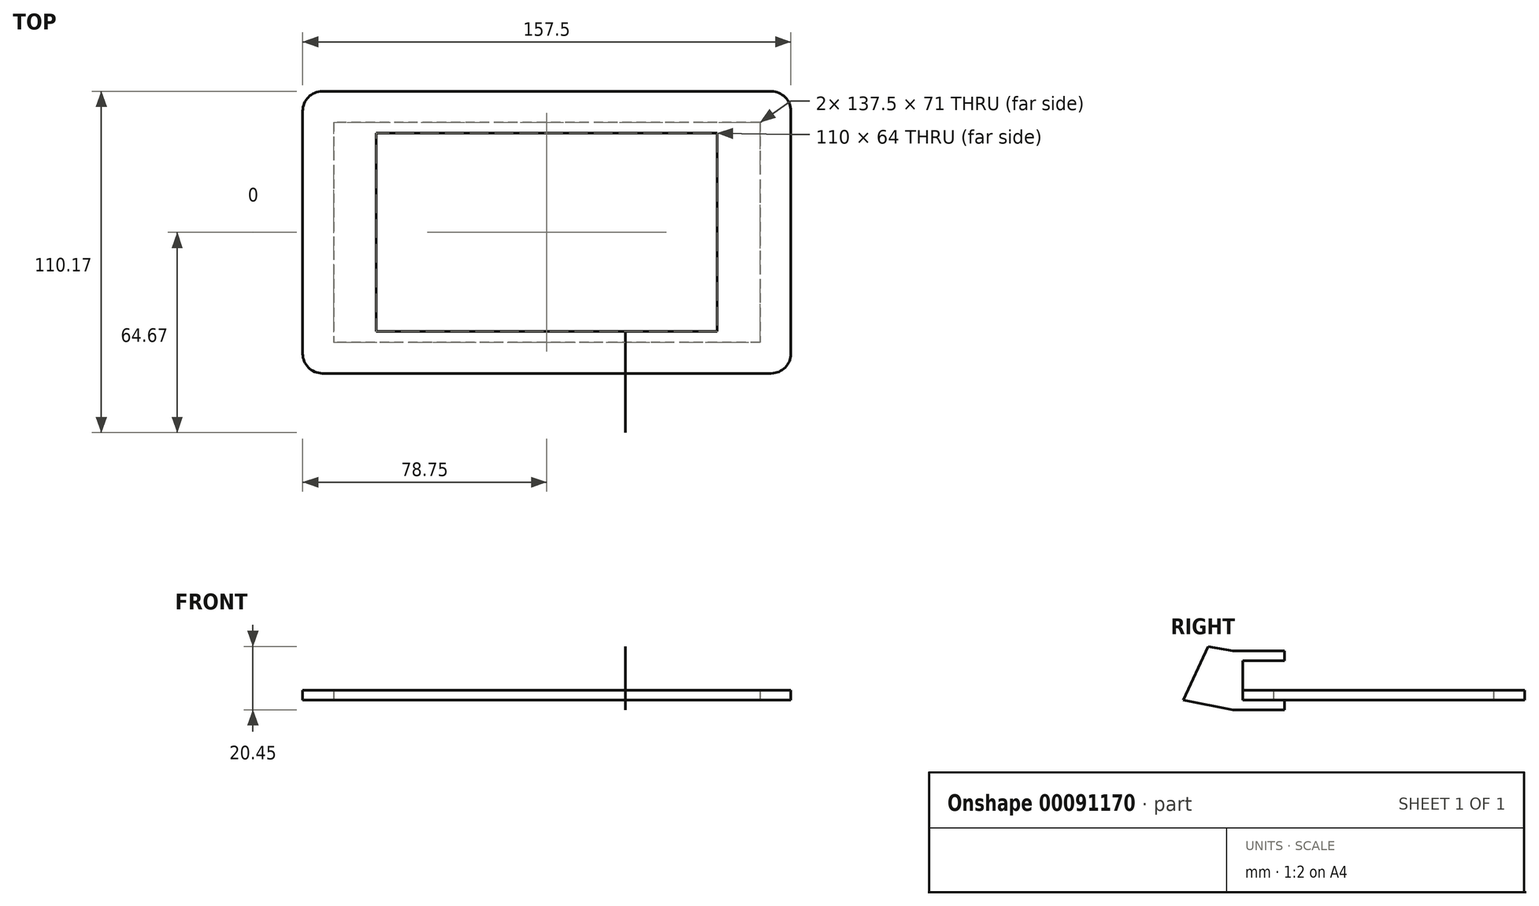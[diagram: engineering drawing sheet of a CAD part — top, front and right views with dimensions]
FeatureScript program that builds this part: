
annotation { "Feature Type Name" : "Feature", "Feature Type Description" : "" }
export const myFeature = defineFeature(function(context is Context, id is Id, definition is map)
    precondition{}
    {
        {
            var Q0;
            Q0=qCreatedBy(makeId("Top.planeOp"),FACE);
            var sketch = newSketch(context, id + "F0", { "sketchPlane" : qUnion([Q0])});
            skLineSegment(sketch, "E0.bottom", {"start": v(55, 32) * mm, "end": v(-55, 32) * mm});
            skLineSegment(sketch, "E0.top", {"start": v(55, -32) * mm, "end": v(-55, -32) * mm});
            skLineSegment(sketch, "E0.left", {"start": v(55, 32) * mm, "end": v(55, -32) * mm});
            skLineSegment(sketch, "E0.right", {"start": v(-55, 32) * mm, "end": v(-55, -32) * mm});
            skPoint(sketch, "E0.middle", {"position": v(0, 0) * mm});
            skLineSegment(sketch, "E1.bottom", {"start": v(68.75, 35.5) * mm, "end": v(-68.75, 35.5) * mm});
            skLineSegment(sketch, "E1.top", {"start": v(68.75, -35.5) * mm, "end": v(-68.75, -35.5) * mm});
            skLineSegment(sketch, "E1.left", {"start": v(68.75, 35.5) * mm, "end": v(68.75, -35.5) * mm});
            skLineSegment(sketch, "E1.right", {"start": v(-68.75, 35.5) * mm, "end": v(-68.75, -35.5) * mm});
            skLineSegment(sketch, "E2.bottom", {"start": v(72.4, 45.5) * mm, "end": v(-72.4, 45.5) * mm});
            skLineSegment(sketch, "E2.top", {"start": v(72.4, -45.5) * mm, "end": v(-72.4, -45.5) * mm});
            skLineSegment(sketch, "E2.left", {"start": v(78.75, 39.15) * mm, "end": v(78.75, -39.15) * mm});
            skLineSegment(sketch, "E2.right", {"start": v(-78.75, 39.15) * mm, "end": v(-78.75, -39.15) * mm});
            skLineSegment(sketch, "E3", {"start": v(0, -45.5) * mm, "end": v(0, -35.5) * mm});
            skLineSegment(sketch, "E4", {"start": v(68.75, 0) * mm, "end": v(78.75, 0) * mm});
            skLineSegment(sketch, "E5", {"start": v(0, 35.5) * mm, "end": v(0, 45.5) * mm});
            skLineSegment(sketch, "E6", {"start": v(-68.75, 0) * mm, "end": v(-78.75, 0) * mm});
            skPoint(sketch, "E7.visualSharp", {"position": v(-78.75, 45.5) * mm});
            skArc(sketch, "E7.filletArc", {"start": v(-72.4, 45.5) * mm, "mid": v(-76.9, 43.64) * mm, "end": v(-78.75, 39.15) * mm});
            skPoint(sketch, "E8.visualSharp", {"position": v(78.75, 45.5) * mm});
            skArc(sketch, "E8.filletArc", {"start": v(78.75, 39.15) * mm, "mid": v(76.9, 43.64) * mm, "end": v(72.4, 45.5) * mm});
            skPoint(sketch, "E9.visualSharp", {"position": v(78.75, -45.5) * mm});
            skArc(sketch, "E9.filletArc", {"start": v(72.4, -45.5) * mm, "mid": v(76.9, -43.64) * mm, "end": v(78.75, -39.15) * mm});
            skPoint(sketch, "E10.visualSharp", {"position": v(-78.75, -45.5) * mm});
            skArc(sketch, "E10.filletArc", {"start": v(-78.75, -39.15) * mm, "mid": v(-76.9, -43.64) * mm, "end": v(-72.4, -45.5) * mm});
            skSolve(sketch);
        }
        {
            var Q0;
            Q0 = qSketchRegion(id + "F0", true);
            var Q1;
            Q1=makeQuery(id+"F0.imprint","IMPRINT",FACE,{"disambiguationData":[TD([[makeQuery(id+"F0.imprint","IMPRINT",EDGE,{"derivedFrom":sQuery(id+"F0.wireOp",EDGE,"E0.bottom")}),-1.0]])]});
            var Q2;
            Q2=makeQuery(id+"F0.imprint","IMPRINT",FACE,{"disambiguationData":[TD([[makeQuery(id+"F0.imprint","IMPRINT",EDGE,{"derivedFrom":sQuery(id+"F0.wireOp",EDGE,"E0.bottom")}),1.0]])]});
            extrude(context, id + "F1", {"entities" : qUnion([Q0, Q1, Q2]), "depth" : 1 / 203.2 * mm});
        }
        {
            var Q0;
            Q0=makeQuery(id+"F1.opExtrude","CAP_FACE",FACE,{"disambiguationData":[OSD([sQuery(id+"F0.wireOp",EDGE,"E2.bottom"),sQuery(id+"F0.wireOp",EDGE,"E2.top"),sQuery(id+"F0.wireOp",EDGE,"E2.left"),sQuery(id+"F0.wireOp",EDGE,"E2.right"),sQuery(id+"F0.wireOp",EDGE,"E7.filletArc"),sQuery(id+"F0.wireOp",EDGE,"E8.filletArc"),sQuery(id+"F0.wireOp",EDGE,"E9.filletArc"),sQuery(id+"F0.wireOp",EDGE,"E10.filletArc")])],"isStart":false});
            var sketch = newSketch(context, id + "F2", { "sketchPlane" : qUnion([Q0])});
            skArc(sketch, "E11.0.0", {"start": v(72.4, -45.5) * mm, "mid": v(76.9, -43.64) * mm, "end": v(78.75, -39.15) * mm});
            skLineSegment(sketch, "E11.0.1", {"start": v(78.75, -39.15) * mm, "end": v(78.75, 39.15) * mm});
            skArc(sketch, "E11.0.2", {"start": v(78.75, 39.15) * mm, "mid": v(76.9, 43.64) * mm, "end": v(72.4, 45.5) * mm});
            skLineSegment(sketch, "E11.0.3", {"start": v(72.4, 45.5) * mm, "end": v(-72.4, 45.5) * mm});
            skArc(sketch, "E11.0.4", {"start": v(-72.4, 45.5) * mm, "mid": v(-76.9, 43.64) * mm, "end": v(-78.75, 39.15) * mm});
            skLineSegment(sketch, "E11.0.5", {"start": v(-78.75, 39.15) * mm, "end": v(-78.75, -39.15) * mm});
            skArc(sketch, "E11.0.6", {"start": v(-78.75, -39.15) * mm, "mid": v(-76.9, -43.64) * mm, "end": v(-72.4, -45.5) * mm});
            skLineSegment(sketch, "E11.0.7", {"start": v(-72.4, -45.5) * mm, "end": v(72.4, -45.5) * mm});
            skLineSegment(sketch, "E12.0", {"start": v(-68.75, 35.5) * mm, "end": v(-68.75, -35.5) * mm});
            skLineSegment(sketch, "E13.0", {"start": v(68.75, 35.5) * mm, "end": v(-68.75, 35.5) * mm});
            skLineSegment(sketch, "E14.0", {"start": v(68.75, 35.5) * mm, "end": v(68.75, -35.5) * mm});
            skLineSegment(sketch, "E15.0", {"start": v(68.75, -35.5) * mm, "end": v(-68.75, -35.5) * mm});
            skSolve(sketch);
        }
        {
            var Q0;
            Q0 = qSketchRegion(id + "F2", true);
            extrude(context, id + "F3", {"entities" : qUnion([Q0]), "depth" : 3.17 * mm});
        }
        {
            var Q0;
            Q0=makeQuery(id+"F3.opExtrude","CAP_FACE",FACE,{"disambiguationData":[OSD([sQuery(id+"F2.wireOp",EDGE,"E11.0.0"),sQuery(id+"F2.wireOp",EDGE,"E11.0.1"),sQuery(id+"F2.wireOp",EDGE,"E11.0.2"),sQuery(id+"F2.wireOp",EDGE,"E11.0.3"),sQuery(id+"F2.wireOp",EDGE,"E11.0.4"),sQuery(id+"F2.wireOp",EDGE,"E11.0.5"),sQuery(id+"F2.wireOp",EDGE,"E11.0.6"),sQuery(id+"F2.wireOp",EDGE,"E11.0.7"),sQuery(id+"F2.wireOp",EDGE,"E12.0"),sQuery(id+"F2.wireOp",EDGE,"E13.0"),sQuery(id+"F2.wireOp",EDGE,"E14.0"),sQuery(id+"F2.wireOp",EDGE,"E15.0")])],"isStart":false});
            var sketch = newSketch(context, id + "F4", { "sketchPlane" : qUnion([Q0])});
            skSolve(sketch);
        }
        {
            var Q0;
            Q0=makeQuery(id+"F4.imprint","IMPRINT",FACE,{"disambiguationData":[TD([[makeQuery(id+"F4.imprint","IMPRINT",EDGE,{"derivedFrom":makeQuery(id+"F3.opExtrude","CAP_EDGE",EDGE,{"disambiguationData":[OSD([sQuery(id+"F2.wireOp",EDGE,"E11.0.0")])],"isStart":false})}),1.0]])]});
            extrude(context, id + "F5", {"entities" : qUnion([Q0]), "depth" : 1 / 203.2 * mm});
        }
        {
            var Q0;
            Q0=makeQuery(id+"F5.opExtrude","CAP_FACE",FACE,{"disambiguationData":[OSD([sQuery(id+"F2.wireOp",EDGE,"E11.0.0"),sQuery(id+"F2.wireOp",EDGE,"E11.0.1"),sQuery(id+"F2.wireOp",EDGE,"E11.0.2"),sQuery(id+"F2.wireOp",EDGE,"E11.0.3"),sQuery(id+"F2.wireOp",EDGE,"E11.0.4"),sQuery(id+"F2.wireOp",EDGE,"E11.0.5"),sQuery(id+"F2.wireOp",EDGE,"E11.0.6"),sQuery(id+"F2.wireOp",EDGE,"E11.0.7"),sQuery(id+"F2.wireOp",EDGE,"E12.0"),sQuery(id+"F2.wireOp",EDGE,"E13.0"),sQuery(id+"F2.wireOp",EDGE,"E14.0"),sQuery(id+"F2.wireOp",EDGE,"E15.0")])],"isStart":false});
            var sketch = newSketch(context, id + "F6", { "sketchPlane" : qUnion([Q0])});
            skArc(sketch, "E16.0.0", {"start": v(72.4, -45.5) * mm, "mid": v(76.9, -43.64) * mm, "end": v(78.75, -39.15) * mm});
            skLineSegment(sketch, "E16.0.1", {"start": v(78.75, -39.15) * mm, "end": v(78.75, 39.15) * mm});
            skArc(sketch, "E16.0.2", {"start": v(78.75, 39.15) * mm, "mid": v(76.9, 43.64) * mm, "end": v(72.4, 45.5) * mm});
            skLineSegment(sketch, "E16.0.3", {"start": v(72.4, 45.5) * mm, "end": v(-72.4, 45.5) * mm});
            skArc(sketch, "E16.0.4", {"start": v(-72.4, 45.5) * mm, "mid": v(-76.9, 43.64) * mm, "end": v(-78.75, 39.15) * mm});
            skLineSegment(sketch, "E16.0.5", {"start": v(-78.75, 39.15) * mm, "end": v(-78.75, -39.15) * mm});
            skArc(sketch, "E16.0.6", {"start": v(-78.75, -39.15) * mm, "mid": v(-76.9, -43.64) * mm, "end": v(-72.4, -45.5) * mm});
            skLineSegment(sketch, "E16.0.7", {"start": v(-72.4, -45.5) * mm, "end": v(72.4, -45.5) * mm});
            skLineSegment(sketch, "E17.0", {"start": v(-55, 32) * mm, "end": v(-55, -32) * mm});
            skLineSegment(sketch, "E18.0", {"start": v(55, 32) * mm, "end": v(-55, 32) * mm});
            skLineSegment(sketch, "E19.0", {"start": v(55, 32) * mm, "end": v(55, -32) * mm});
            skLineSegment(sketch, "E20.0", {"start": v(55, -32) * mm, "end": v(-55, -32) * mm});
            skSolve(sketch);
        }
        {
            var Q0;
            Q0 = qSketchRegion(id + "F6", true);
            extrude(context, id + "F7", {"entities" : qUnion([Q0]), "depth" : 1 / 203.2 * mm});
        }
        {
            var Q0;
            Q0=makeQuery(id+"F1.opExtrude","SWEPT_FACE",FACE,{"disambiguationData":[OSD([sQuery(id+"F0.wireOp",EDGE,"E2.top")])]});
            var sketch = newSketch(context, id + "F8", { "sketchPlane" : qUnion([Q0])});
            skLineSegment(sketch, "E21", {"start": v(0, 0) * mm, "end": v(25.4, 0) * mm});
            skLineSegment(sketch, "E22", {"start": v(0, 0) * mm, "end": v(-25.4, 0) * mm});
            skLineSegment(sketch, "E23", {"start": v(0, 0) * mm, "end": v(-12.7, 0) * mm});
            skLineSegment(sketch, "E24", {"start": v(0, 0) * mm, "end": v(12.7, 0) * mm});
            skSolve(sketch);
        }
        {
            var Q0;
            Q0=sQuery(id+"F0.wireOp",EDGE,"E2.top");
            var Q1;
            Q1=sQuery(id+"F8.wireOp",VERTEX,"E21.start");
            cPlane(context, id + "F9", {"entities" : qUnion([Q0, Q1]), "cplaneType" : CPlaneType.LINE_POINT, "offset" : 152.4 * mm, "width" : 152.4 * mm, "height" : 152.4 * mm});
        }
        {
            var Q0;
            Q0=qCreatedBy(id+"F9.planeOp",FACE);
            var sketch = newSketch(context, id + "F10", { "sketchPlane" : qUnion([Q0])});
            skPoint(sketch, "E25.0", {"position": v(45.5, 12.7) * mm});
            skPoint(sketch, "E26.0", {"position": v(32, 0) * mm});
            skLineSegment(sketch, "E27", {"start": v(45.5, 12.7) * mm, "end": v(45.5, 0) * mm});
            skLineSegment(sketch, "E28", {"start": v(45.5, 0) * mm, "end": v(32, 0) * mm});
            skLineSegment(sketch, "E29", {"start": v(32, -3.18) * mm, "end": v(48.68, -3.17) * mm});
            skLineSegment(sketch, "E30", {"start": v(48.67, -3.18) * mm, "end": v(64.67, 0) * mm});
            skLineSegment(sketch, "E31", {"start": v(32, -3.18) * mm, "end": v(32, 0) * mm});
            skLineSegment(sketch, "E32", {"start": v(45.5, 12.7) * mm, "end": v(32, 12.7) * mm});
            skLineSegment(sketch, "E33", {"start": v(32, 12.7) * mm, "end": v(32, 15.88) * mm});
            skLineSegment(sketch, "E34", {"start": v(32, 15.88) * mm, "end": v(48.68, 15.88) * mm});
            skLineSegment(sketch, "E35", {"start": v(48.67, 15.88) * mm, "end": v(56.66, 17.28) * mm});
            skLineSegment(sketch, "E36", {"start": v(56.66, 17.28) * mm, "end": v(64.67, 0) * mm});
            skLineSegment(sketch, "E37", {"start": v(48.68, -3.17) * mm, "end": v(48.68, 15.88) * mm});
            skLineSegment(sketch, "E38", {"start": v(45.5, 6.35) * mm, "end": v(48.68, 6.35) * mm, "construction": true});
            skSolve(sketch);
        }
        {
            var Q0;
            Q0=sQuery(id+"F0.wireOp",EDGE,"E2.top");
            var Q1;
            Q1=sQuery(id+"F8.wireOp",VERTEX,"E21.end");
            cPlane(context, id + "F11", {"entities" : qUnion([Q0, Q1]), "cplaneType" : CPlaneType.LINE_POINT, "offset" : 152.4 * mm, "width" : 152.4 * mm, "height" : 152.4 * mm});
        }
        {
            var Q0;
            Q0=qCreatedBy(id+"F11.planeOp",FACE);
            var sketch = newSketch(context, id + "F12", { "sketchPlane" : qUnion([Q0])});
            skLineSegment(sketch, "E39.0.0", {"start": v(48.68, 15.88) * mm, "end": v(48.68, -3.17) * mm});
            skLineSegment(sketch, "E39.0.1", {"start": v(48.67, -3.18) * mm, "end": v(64.67, 0) * mm});
            skLineSegment(sketch, "E39.0.2", {"start": v(64.67, 0) * mm, "end": v(56.66, 17.28) * mm});
            skLineSegment(sketch, "E39.0.3", {"start": v(56.66, 17.28) * mm, "end": v(48.67, 15.87) * mm});
            skLineSegment(sketch, "E39.1.0", {"start": v(32, 12.7) * mm, "end": v(45.5, 12.7) * mm});
            skLineSegment(sketch, "E39.1.1", {"start": v(45.5, 12.7) * mm, "end": v(45.5, 0) * mm});
            skLineSegment(sketch, "E39.1.2", {"start": v(45.5, 0) * mm, "end": v(32, 0) * mm});
            skLineSegment(sketch, "E39.1.3", {"start": v(32, 0) * mm, "end": v(32, -3.18) * mm});
            skLineSegment(sketch, "E39.1.4", {"start": v(32, -3.18) * mm, "end": v(48.68, -3.17) * mm});
            skLineSegment(sketch, "E39.1.5", {"start": v(48.68, -3.17) * mm, "end": v(48.68, 15.88) * mm});
            skLineSegment(sketch, "E39.1.6", {"start": v(48.68, 15.88) * mm, "end": v(32, 15.88) * mm});
            skLineSegment(sketch, "E39.1.7", {"start": v(32, 15.88) * mm, "end": v(32, 12.7) * mm});
            skSolve(sketch);
        }
        {
            var Q0;
            Q0 = qSketchRegion(id + "F12", true);
            extrude(context, id + "F13", {"entities" : qUnion([Q0]), "depth" : 1 / 203.2 * mm});
        }
        {
            var Q0;
            Q0=sQuery(id+"F8.wireOp",VERTEX,"E24.end");
            var Q1;
            Q1=sQuery(id+"F8.wireOp",EDGE,"E21");
            cPlane(context, id + "F14", {"entities" : qUnion([Q0, Q1]), "cplaneType" : CPlaneType.LINE_POINT, "offset" : 152.4 * mm, "width" : 152.4 * mm, "height" : 152.4 * mm});
        }
    });
